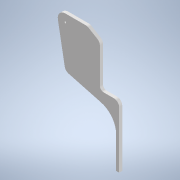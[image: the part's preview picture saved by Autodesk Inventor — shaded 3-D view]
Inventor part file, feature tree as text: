
AUTODESK INVENTOR PART (.ipt)
format: ipt  version: 2020 (Build 240168000, 168)  size: 141,312 bytes
history: native  units: mm
features: other x4, sketch x2
ambient origin geometry x8: Origin, YZ Plane, XZ Plane, XY Plane, X Axis, Y Axis, Z Axis, Center Point
bodies: Body1 (feature_tree)
feature tree (6):
  other  "guarra.ipt"
  sketch  "Esboço2"
  other  "Sólido1::guarra.ipt"
  other  "OperaçãoIdentificador1"
  sketch  "Esboço1"  dims[d0=10.0mm]
  other  "Sólido1"
